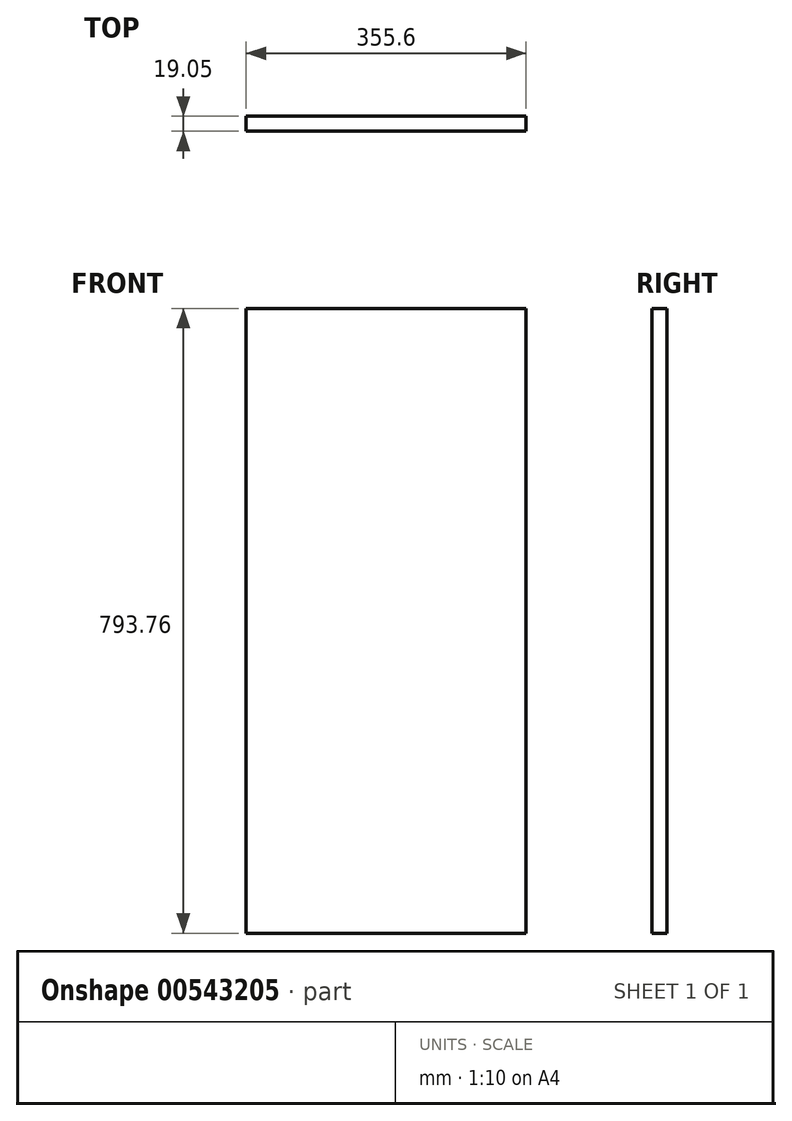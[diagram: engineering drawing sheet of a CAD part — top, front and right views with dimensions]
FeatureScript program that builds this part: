
annotation { "Feature Type Name" : "Feature", "Feature Type Description" : "" }
export const myFeature = defineFeature(function(context is Context, id is Id, definition is map)
    precondition{}
    {
        {
            var Q0;
            Q0=qCreatedBy(makeId("Front.planeOp"),FACE);
            var sketch = newSketch(context, id + "F0", { "sketchPlane" : qUnion([Q0])});
            skLineSegment(sketch, "E0.bottom", {"start": v(177.8, 396.88) * mm, "end": v(-177.8, 396.88) * mm});
            skLineSegment(sketch, "E0.top", {"start": v(177.8, -396.88) * mm, "end": v(-177.8, -396.88) * mm});
            skLineSegment(sketch, "E0.left", {"start": v(177.8, 396.88) * mm, "end": v(177.8, -396.88) * mm});
            skLineSegment(sketch, "E0.right", {"start": v(-177.8, 396.88) * mm, "end": v(-177.8, -396.88) * mm});
            skPoint(sketch, "E0.middle", {"position": v(0, 0) * mm});
            skSolve(sketch);
        }
        {
            var Q0;
            Q0 = qSketchRegion(id + "F0", true);
            extrude(context, id + "F1", {"entities" : qUnion([Q0]), "depth" : 19.05 * mm, "offsetDistance" : 25.4 * mm});
        }
    });
